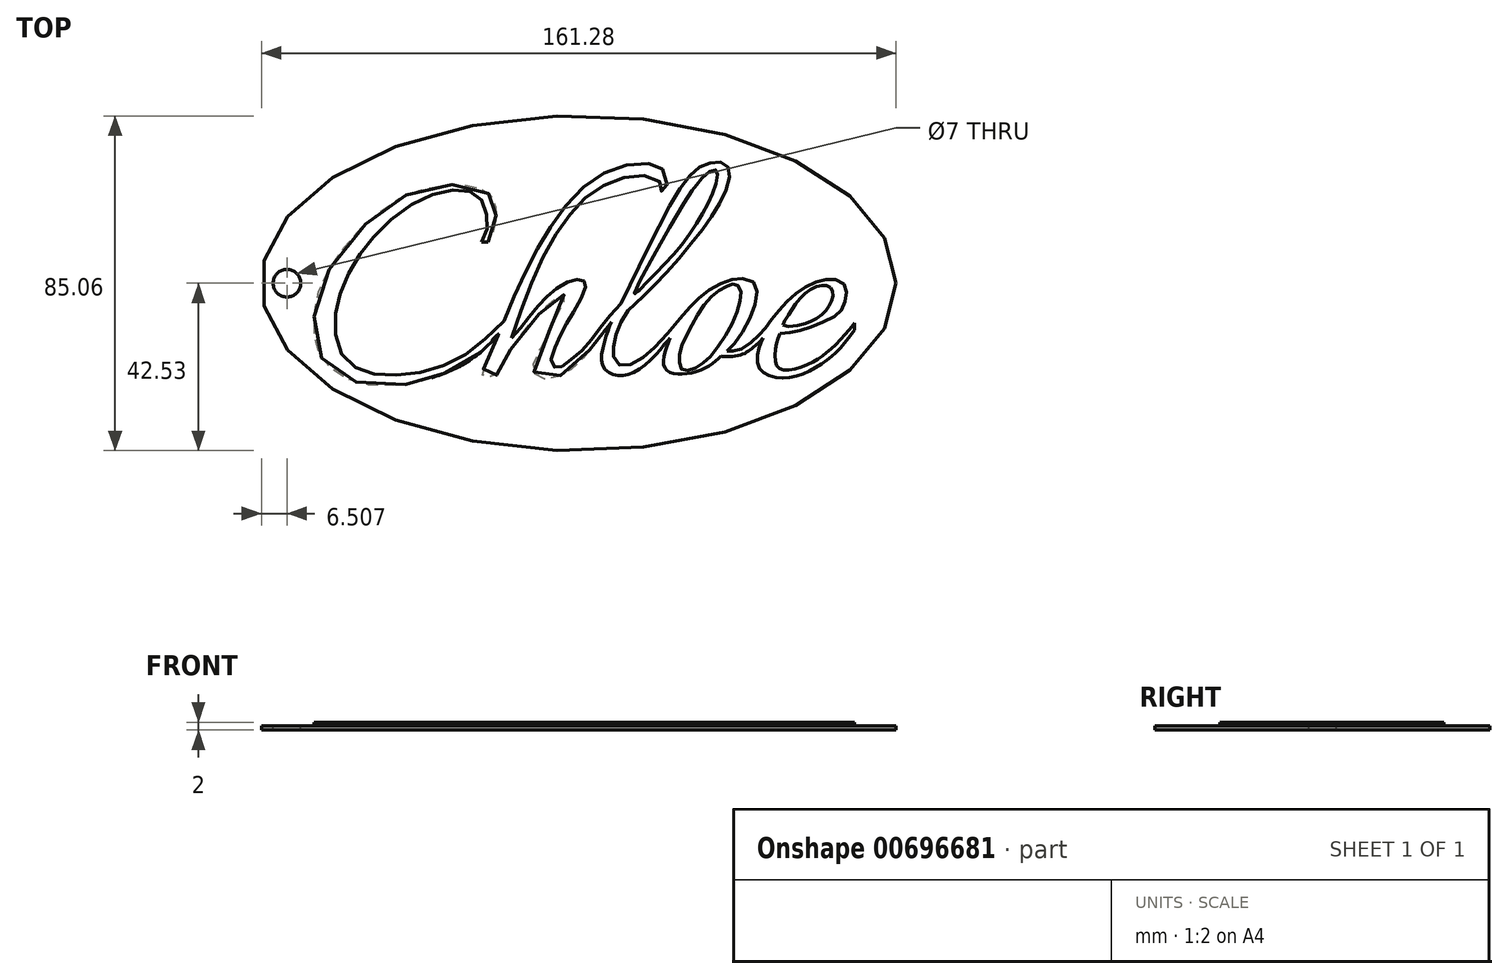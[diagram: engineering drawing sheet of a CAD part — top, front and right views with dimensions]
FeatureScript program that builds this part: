
annotation { "Feature Type Name" : "Feature", "Feature Type Description" : "" }
export const myFeature = defineFeature(function(context is Context, id is Id, definition is map)
    precondition{}
    {
        {
            var Q0;
            Q0=qCreatedBy(makeId("Top.planeOp"),FACE);
            var sketch = newSketch(context, id + "F0", { "sketchPlane" : qUnion([Q0])});
            skFitSpline(sketch, "E0", {"points": [v(-24.68, 10.46) * mm, v(-23.31, 13.77) * mm, v(-23.43, 17.64) * mm, v(-24.9, 21.51) * mm, v(-28.1, 23.45) * mm, v(-34.25, 23.34) * mm, v(-42.79, 19.8) * mm, v(-51.44, 12.51) * mm, v(-56.68, 5.57) * mm, v(-60.67, -2.63) * mm, v(-61.92, -9.92) * mm, v(-60.56, -17.56) * mm, v(-55.43, -22.11) * mm, v(-48.03, -23.36) * mm, v(-37.66, -22) * mm, v(-27.87, -17.44) * mm, v(-18.98, -9.58) * mm], "startDerivative": vector(38.97, 73.87) * mm, "endDerivative": vector(108.55, 107.4) * mm});
            skFitSpline(sketch, "E1", {"points": [v(-18.98, -9.58) * mm, v(-14.88, 0) * mm, v(-10.21, 9.33) * mm, v(-5.09, 17.3) * mm, v(1.75, 24.93) * mm, v(9.26, 29.14) * mm, v(17, 30.51) * mm, v(20.77, 29.37) * mm, v(22.25, 26.98) * mm, v(21.9, 23.1) * mm, v(21, 23.45) * mm, v(21.1, 24.7) * mm, v(19.63, 26.52) * mm, v(14.85, 27.32) * mm, v(8.47, 25.84) * mm, v(2.09, 22.08) * mm, v(-2.8, 16.62) * mm, v(-7.93, 8.76) * mm, v(-12.83, -2.06) * mm, v(-17.05, -13.91) * mm], "startDerivative": vector(59.11, 142.43) * mm, "endDerivative": vector(-54.93, -161.28) * mm});
            skFitSpline(sketch, "E2", {"points": [v(-17.05, -13.91) * mm, v(-13.4, -9.58) * mm, v(-9.53, -4.8) * mm, v(-5.77, -1.5) * mm, v(-1.83, 0.7) * mm, v(0.53, 0.95) * mm, v(1.59, 0.36) * mm, v(1.7, -1.18) * mm, v(-1.06, -6.7) * mm, v(-3.85, -11.63) * mm, v(-6.24, -16.85) * mm, v(-6.91, -20.49) * mm, v(-5.38, -21.54) * mm, v(-3.13, -20.34) * mm, v(1.57, -16.37) * mm, v(5.44, -11.3) * mm, v(10.76, -5.11) * mm], "startDerivative": vector(50.61, 58.34) * mm, "endDerivative": vector(66.05, 72.47) * mm});
            skFitSpline(sketch, "E3", {"points": [v(10.76, -5.11) * mm, v(18.42, 10.58) * mm, v(27.27, 26.2) * mm, v(32.1, 30.15) * mm, v(36.46, 30.64) * mm, v(38.3, 28.38) * mm, v(36.46, 21.7) * mm, v(31.46, 13.72) * mm, v(22.6, 3.17) * mm, v(15.76, -3.92) * mm, v(12.46, -6.98) * mm], "startDerivative": vector(51.1, 106.1) * mm, "endDerivative": vector(-42.36, -38.24) * mm});
            skFitSpline(sketch, "E4", {"points": [v(12.46, -6.98) * mm, v(10.04, -11.25) * mm, v(8.83, -16) * mm, v(8.83, -18.74) * mm, v(10.76, -20.91) * mm, v(15.03, -19.78) * mm, v(20.19, -15.43) * mm, v(26.87, -7.62) * mm, v(30.1, -4.16) * mm, v(34.28, -1.02) * mm, v(38.39, 0.84) * mm, v(41.45, 1.16) * mm, v(44.75, 0) * mm, v(45.07, -3.76) * mm, v(43.46, -8.9) * mm, v(40, -14.7) * mm, v(37.66, -17.29) * mm], "startDerivative": vector(-42.02, -63.3) * mm, "endDerivative": vector(-41.58, -41.12) * mm});
            skFitSpline(sketch, "E5", {"points": [v(37.66, -17.29) * mm, v(38.8, -17.29) * mm, v(41.33, -16.65) * mm, v(45.07, -13.91) * mm, v(47.4, -11.4) * mm, v(49.98, -7.97) * mm, v(53.52, -4.03) * mm, v(57.43, -1.09) * mm, v(61.7, 0.72) * mm, v(64.88, 1) * mm, v(67.62, -0.52) * mm, v(67.86, -3.26) * mm, v(67.06, -6.4) * mm, v(64.56, -8.62) * mm, v(59, -11.15) * mm, v(54.9, -12.28) * mm, v(51.07, -12.77) * mm], "startDerivative": vector(29.79, -1.25) * mm, "endDerivative": vector(-60.5, -6.1) * mm});
            skFitSpline(sketch, "E6", {"points": [v(51.07, -12.77) * mm, v(50, -16.55) * mm, v(50.17, -20.71) * mm, v(51.86, -22.04) * mm, v(56.61, -21.32) * mm, v(61, -19.06) * mm, v(64.22, -16.55) * mm, v(68.3, -12.3) * mm, v(70.02, -10.12) * mm], "startDerivative": vector(-10.08, -28.83) * mm, "endDerivative": vector(14.2, 18.8) * mm});
            skFitSpline(sketch, "E7", {"points": [v(70.02, -10.12) * mm, v(70.02, -11.9) * mm], "startDerivative": vector(0, -1.77) * mm, "endDerivative": vector(0, -1.77) * mm});
            skFitSpline(sketch, "E8", {"points": [v(70.02, -11.9) * mm, v(68.77, -13.59) * mm, v(66.36, -16.55) * mm, v(63.9, -18.86) * mm, v(60.72, -21.08) * mm, v(56.53, -23.17) * mm, v(52.3, -24.1) * mm, v(47.95, -23.3) * mm, v(45.62, -21.08) * mm, v(45.74, -16.55) * mm, v(46.83, -13.91) * mm], "startDerivative": vector(-14.9, -20.54) * mm, "endDerivative": vector(13.5, 26.36) * mm});
            skFitSpline(sketch, "E9", {"points": [v(46.83, -13.91) * mm, v(45.7, -15.12) * mm, v(43.65, -16.85) * mm, v(41.1, -18.22) * mm, v(37.32, -18.62) * mm, v(36.2, -18.54) * mm], "startDerivative": vector(-6.05, -6.9) * mm, "endDerivative": vector(-6.62, 0.78) * mm});
            skFitSpline(sketch, "E10", {"points": [v(51.9, -10.65) * mm, v(53.07, -8.43) * mm, v(55.08, -5.25) * mm, v(57.9, -2.3) * mm, v(60.96, -0.7) * mm, v(62.98, -0.62) * mm, v(64.18, -1.34) * mm, v(64.55, -3) * mm, v(63.86, -5.25) * mm, v(62.5, -7.34) * mm, v(59.87, -9.24) * mm, v(56.65, -10.48) * mm, v(51.9, -10.65) * mm]});
            skFitSpline(sketch, "E11", {"points": [v(36.2, -18.54) * mm, v(34.47, -20.03) * mm, v(32, -21.63) * mm, v(28.47, -22.82) * mm, v(25.05, -23.02) * mm, v(22.8, -22.5) * mm, v(21.63, -20.8) * mm, v(21.75, -18.2) * mm, v(22.69, -15.22) * mm, v(23.17, -13.91) * mm], "startDerivative": vector(-15.8, -14.4) * mm, "endDerivative": vector(5.34, 14.23) * mm});
            skFitSpline(sketch, "E12", {"points": [v(25.56, -20.12) * mm, v(25.73, -17.44) * mm, v(27.24, -13.5) * mm, v(29.78, -8.78) * mm, v(32.77, -4.37) * mm, v(35.76, -1.72) * mm, v(38.06, -0.55) * mm, v(39.54, -0.24) * mm, v(40.71, -0.87) * mm, v(41.2, -2.97) * mm, v(40.14, -7.47) * mm, v(37.07, -13.57) * mm, v(33.28, -18.72) * mm, v(30.4, -21.08) * mm, v(27.87, -22.2) * mm, v(26.16, -21.91) * mm, v(25.56, -20.12) * mm]});
            skFitSpline(sketch, "E13", {"points": [v(23.17, -13.91) * mm, v(21.67, -15.68) * mm, v(17.95, -19.74) * mm, v(13.38, -22.93) * mm, v(10.1, -23.44) * mm, v(7.65, -22.72) * mm, v(5.93, -20.46) * mm, v(6.1, -16.6) * mm, v(7.28, -12.36) * mm, v(8.3, -9.86) * mm], "startDerivative": vector(-14.93, -17.64) * mm, "endDerivative": vector(10.52, 24.03) * mm});
            skFitSpline(sketch, "E14", {"points": [v(8.3, -9.86) * mm, v(6.47, -11.75) * mm, v(3.25, -16.36) * mm, v(-0.88, -21) * mm, v(-4.78, -23.54) * mm, v(-8.6, -24.35) * mm, v(-10.87, -23.47) * mm, v(-11.55, -21.2) * mm, v(-10.4, -18.09) * mm, v(-3.9, -4.91) * mm, v(-3.35, -3.7) * mm, v(-3.8, -2.91) * mm, v(-5.01, -3.32) * mm, v(-7.08, -4.98) * mm, v(-12.73, -10.6) * mm, v(-16.8, -16.02) * mm, v(-19.68, -20.8) * mm, v(-20.15, -22.39) * mm, v(-20.92, -23.37) * mm, v(-22.58, -23.7) * mm, v(-24.24, -23.54) * mm, v(-24.5, -22.86) * mm, v(-23.52, -20.35) * mm, v(-21.4, -15.34) * mm, v(-20.4, -12.94) * mm, v(-22.03, -14.5) * mm, v(-24.13, -16.83) * mm, v(-29.28, -20.6) * mm, v(-34.04, -22.84) * mm, v(-39.65, -24.84) * mm, v(-45.57, -25.89) * mm, v(-54.96, -25.56) * mm, v(-61.13, -22.99) * mm, v(-65.46, -18.72) * mm, v(-67.02, -13.91) * mm, v(-66.88, -5.38) * mm, v(-64.04, 2.41) * mm, v(-57.06, 12.1) * mm, v(-49.34, 19) * mm, v(-42.7, 22.87) * mm, v(-34.98, 24.76) * mm, v(-27.67, 24.83) * mm, v(-23.45, 23.23) * mm, v(-22.05, 21.75) * mm, v(-21.2, 19.62) * mm, v(-21, 17.77) * mm, v(-21.05, 15.54) * mm, v(-22.25, 11.96) * mm, v(-23.06, 10.4) * mm], "startDerivative": vector(-108.62, -99.66) * mm, "endDerivative": vector(-54.33, -108.22) * mm});
            skFitSpline(sketch, "E15", {"points": [v(-24.68, 10.46) * mm, v(-23.06, 10.4) * mm], "startDerivative": vector(1.61, -0.06) * mm, "endDerivative": vector(1.61, -0.06) * mm});
            skFitSpline(sketch, "E16", {"points": [v(14.2, -2.54) * mm, v(27.88, 22.18) * mm, v(29.77, 24.82) * mm, v(32.41, 27.87) * mm, v(34.65, 28.81) * mm, v(35.2, 28.07) * mm, v(34.65, 24.68) * mm, v(32.62, 19.8) * mm, v(29.57, 14.6) * mm, v(25.23, 8.56) * mm, v(20.15, 3.15) * mm, v(15.76, -1.32) * mm, v(14.2, -2.54) * mm]});
            skSolve(sketch);
        }
        {
            var Q0;
            Q0 = qSketchRegion(id + "F0", true);
            extrude(context, id + "F1", {"entities" : qUnion([Q0]), "depth" : 2 * mm, "offsetDistance" : 25 * mm});
        }
        {
            var Q0;
            Q0=qCreatedBy(makeId("Top.planeOp"),FACE);
            var sketch = newSketch(context, id + "F2", { "sketchPlane" : qUnion([Q0])});
            skEllipse(sketch, "E17", {"center": v(0, 0) * mm, "majorRadius": 80.64 * mm, "minorRadius": 42.53 * mm, "majorAxis": v(1, 0)});
            skSolve(sketch);
        }
        {
            var Q0;
            Q0 = qSketchRegion(id + "F2", true);
            extrude(context, id + "F3", {"entities" : qUnion([Q0]), "operationType" : NewBodyOperationType.ADD, "depth" : 1 * mm, "offsetDistance" : 25 * mm});
        }
        {
            var Q0;
            {var subQ0=sQuery(id+"F2.wireOp",EDGE,"E17");Q0=makeQuery(id+"F3.boolean.opBoolean","SPLIT",FACE,{"disambiguationData":[TD([makeQuery(id+"F1.opExtrude","SWEPT_FACE",FACE,{"disambiguationData":[OSD([sQuery(id+"F0.wireOp",EDGE,"E0")])]})])],"derivedFrom":makeQuery(id+"F3.opExtrude","CAP_FACE",FACE,{"disambiguationData":[OSD([subQ0])],"isStart":false})});}
            var sketch = newSketch(context, id + "F4", { "sketchPlane" : qUnion([Q0])});
            skCircle(sketch, "E18", {"center": v(-74.13, 0) * mm, "radius": 3.5 * mm});
            skSolve(sketch);
        }
        {
            var Q0;
            Q0 = qSketchRegion(id + "F4", true);
            extrude(context, id + "F5", {"entities" : qUnion([Q0]), "operationType" : NewBodyOperationType.REMOVE, "oppositeDirection" : true, "depth" : 25 * mm, "offsetDistance" : 25 * mm});
        }
    });
